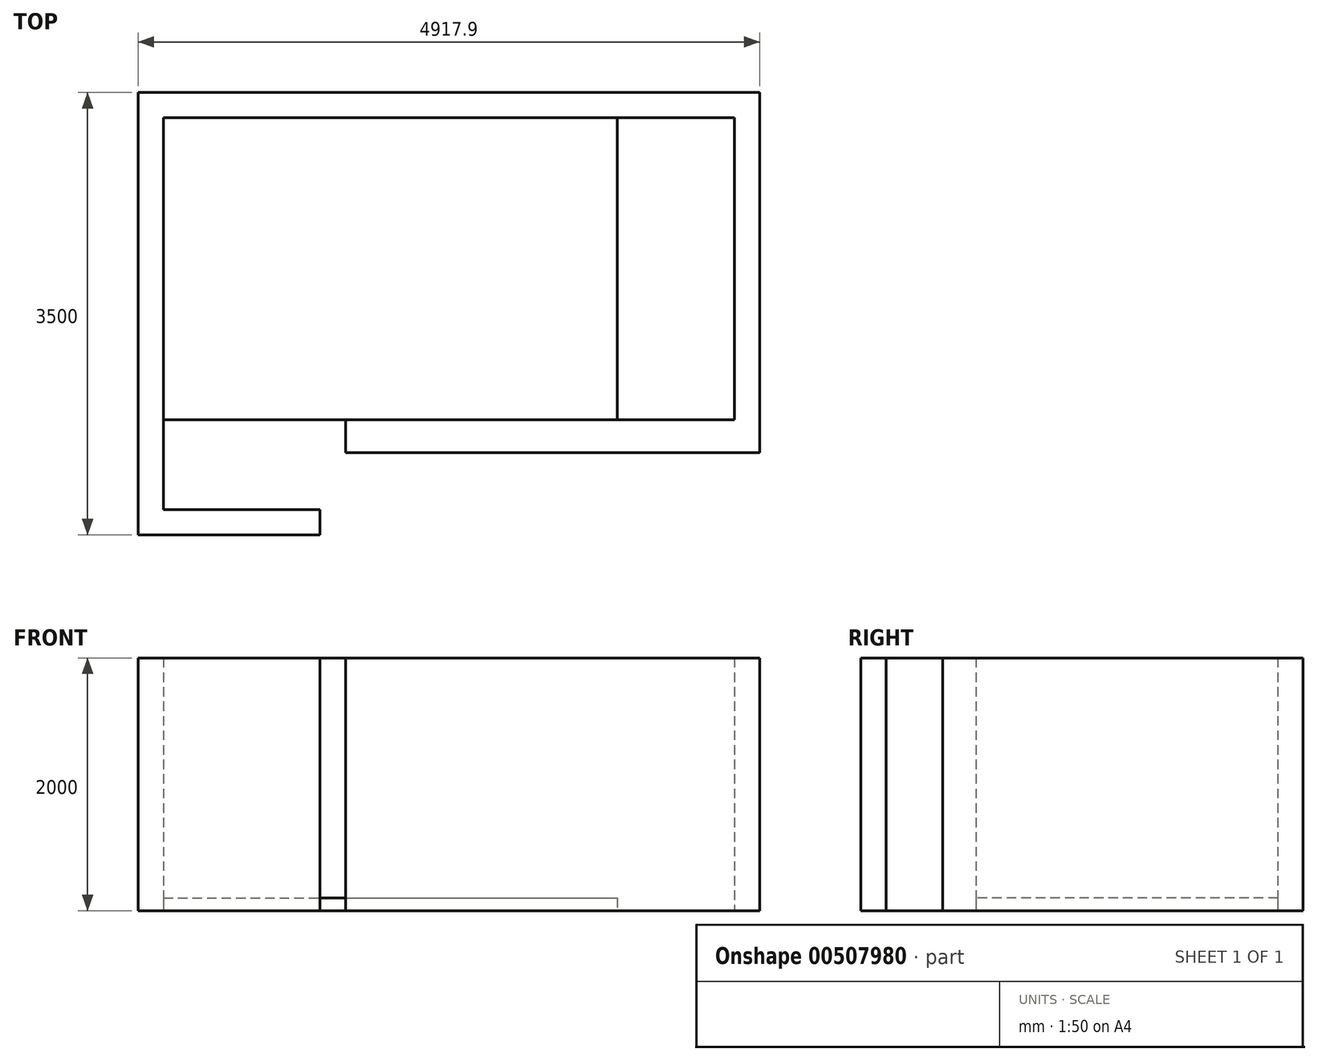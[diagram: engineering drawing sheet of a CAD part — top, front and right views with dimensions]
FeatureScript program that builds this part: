
annotation { "Feature Type Name" : "Feature", "Feature Type Description" : "" }
export const myFeature = defineFeature(function(context is Context, id is Id, definition is map)
    precondition{}
    {
        {
            var Q0;
            Q0=qCreatedBy(makeId("Top.planeOp"),FACE);
            var sketch = newSketch(context, id + "F0", { "sketchPlane" : qUnion([Q0])});
            skLineSegment(sketch, "E0.bottom", {"start": v(-1795, 1195) * mm, "end": v(1795, 1195) * mm});
            skLineSegment(sketch, "E0.top", {"start": v(-1795, -1195) * mm, "end": v(1795, -1195) * mm});
            skLineSegment(sketch, "E0.left", {"start": v(-1795, 1195) * mm, "end": v(-1795, -1195) * mm});
            skLineSegment(sketch, "E0.right", {"start": v(1795, 1195) * mm, "end": v(1795, -1195) * mm});
            skPoint(sketch, "E0.middle", {"position": v(0, 0) * mm});
            skLineSegment(sketch, "E1.bottom", {"start": v(-1795, -1195) * mm, "end": v(-555, -1195) * mm});
            skLineSegment(sketch, "E1.top", {"start": v(-1795, -1905) * mm, "end": v(-555, -1905) * mm});
            skLineSegment(sketch, "E1.left", {"start": v(-1795, -1195) * mm, "end": v(-1795, -1905) * mm});
            skLineSegment(sketch, "E1.right", {"start": v(-555, -1195) * mm, "end": v(-555, -1905) * mm});
            skLineSegment(sketch, "E2.bottom", {"start": v(-1795, 1195) * mm, "end": v(-1995, 1195) * mm});
            skLineSegment(sketch, "E2.top", {"start": v(-1795, -1905) * mm, "end": v(-1995, -1905) * mm});
            skLineSegment(sketch, "E2.left", {"start": v(-1795, 1195) * mm, "end": v(-1795, -1905) * mm});
            skLineSegment(sketch, "E2.right", {"start": v(-1995, 1195) * mm, "end": v(-1995, -1905) * mm});
            skLineSegment(sketch, "E3.bottom", {"start": v(-1995, -1905) * mm, "end": v(-555, -1905) * mm});
            skLineSegment(sketch, "E3.top", {"start": v(-1995, -2105) * mm, "end": v(-555, -2105) * mm});
            skLineSegment(sketch, "E3.left", {"start": v(-1995, -1905) * mm, "end": v(-1995, -2105) * mm});
            skLineSegment(sketch, "E3.right", {"start": v(-555, -1905) * mm, "end": v(-555, -2105) * mm});
            skLineSegment(sketch, "E4.bottom", {"start": v(-555, -1195) * mm, "end": v(-355, -1195) * mm});
            skLineSegment(sketch, "E4.top", {"start": v(-555, -2105) * mm, "end": v(-355, -2105) * mm});
            skLineSegment(sketch, "E4.left", {"start": v(-555, -1195) * mm, "end": v(-555, -2105) * mm});
            skLineSegment(sketch, "E4.right", {"start": v(-355, -1195) * mm, "end": v(-355, -2105) * mm});
            skLineSegment(sketch, "E5.bottom", {"start": v(-355, -1195) * mm, "end": v(2722.9, -1195) * mm});
            skLineSegment(sketch, "E5.top", {"start": v(-355, -1456.6) * mm, "end": v(2722.9, -1456.6) * mm});
            skLineSegment(sketch, "E5.left", {"start": v(-355, -1195) * mm, "end": v(-355, -1456.6) * mm});
            skLineSegment(sketch, "E5.right", {"start": v(2722.9, -1195) * mm, "end": v(2722.9, -1456.6) * mm});
            skLineSegment(sketch, "E6.bottom", {"start": v(2722.9, -1456.6) * mm, "end": v(2922.9, -1456.6) * mm});
            skLineSegment(sketch, "E6.top", {"start": v(2722.9, 1195) * mm, "end": v(2922.9, 1195) * mm});
            skLineSegment(sketch, "E6.left", {"start": v(2722.9, -1456.6) * mm, "end": v(2722.9, 1195) * mm});
            skLineSegment(sketch, "E6.right", {"start": v(2922.9, -1456.6) * mm, "end": v(2922.9, 1195) * mm});
            skLineSegment(sketch, "E7.bottom", {"start": v(-1995, 1195) * mm, "end": v(2922.9, 1195) * mm});
            skLineSegment(sketch, "E7.top", {"start": v(-1995, 1395) * mm, "end": v(2922.9, 1395) * mm});
            skLineSegment(sketch, "E7.left", {"start": v(-1995, 1195) * mm, "end": v(-1995, 1395) * mm});
            skLineSegment(sketch, "E7.right", {"start": v(2922.9, 1195) * mm, "end": v(2922.9, 1395) * mm});
            skSolve(sketch);
        }
        {
            var Q0;
            {var subQ3=sQuery(id+"F0.wireOp",EDGE,"E2.right");Q0=makeQuery(id+"F0.imprint","IMPRINT",FACE,{"disambiguationData":[TD([[makeQuery(id+"F0.imprint","IMPRINT",EDGE,{"derivedFrom":subQ3}),1.0]])]});}
            extrude(context, id + "F1", {"entities" : qUnion([Q0]), "depth" : 2000 * mm});
        }
        {
            var Q0;
            {var subQ1=sQuery(id+"F0.wireOp",EDGE,"E3.top");Q0=makeQuery(id+"F0.imprint","IMPRINT",FACE,{"disambiguationData":[TD([[makeQuery(id+"F0.imprint","IMPRINT",EDGE,{"derivedFrom":subQ1}),1.0]])]});}
            var Q1;
            {var subQ3=sQuery(id+"F0.wireOp",EDGE,"E4.bottom");Q1=makeQuery(id+"F0.imprint","IMPRINT",FACE,{"disambiguationData":[TD([[makeQuery(id+"F0.imprint","IMPRINT",EDGE,{"derivedFrom":subQ3}),-1.0]])]});}
            var Q2;
            {var subQ1=sQuery(id+"F0.wireOp",EDGE,"E5.top");Q2=makeQuery(id+"F0.imprint","IMPRINT",FACE,{"disambiguationData":[TD([[makeQuery(id+"F0.imprint","IMPRINT",EDGE,{"derivedFrom":subQ1}),1.0]])]});}
            var Q3;
            {var subQ5=sQuery(id+"F0.wireOp",EDGE,"E6.bottom");Q3=makeQuery(id+"F0.imprint","IMPRINT",FACE,{"disambiguationData":[TD([[makeQuery(id+"F0.imprint","IMPRINT",EDGE,{"derivedFrom":subQ5}),1.0]])]});}
            var Q4;
            Q4=makeQuery(id+"F0.imprint","IMPRINT",FACE,{"disambiguationData":[TD([[makeQuery(id+"F0.imprint","IMPRINT",EDGE,{"derivedFrom":sQuery(id+"F0.wireOp",EDGE,"E7.top")}),-1.0]])]});
            extrude(context, id + "F2", {"entities" : qUnion([Q0, Q1, Q2, Q3, Q4]), "operationType" : NewBodyOperationType.ADD, "depth" : 2000 * mm});
        }
        {
            var Q0;
            {var subQ0=sQuery(id+"F0.wireOp",EDGE,"E1.bottom");Q0=makeQuery(id+"F0.imprint","IMPRINT",FACE,{"disambiguationData":[TD([[makeQuery(id+"F0.imprint","IMPRINT",EDGE,{"derivedFrom":subQ0}),-1.0]])]});}
            var Q1;
            {var subQ5=sQuery(id+"F0.wireOp",EDGE,"E0.right");Q1=makeQuery(id+"F0.imprint","IMPRINT",FACE,{"disambiguationData":[TD([[makeQuery(id+"F0.imprint","IMPRINT",EDGE,{"derivedFrom":subQ5}),-1.0]])]});}
            extrude(context, id + "F3", {"entities" : qUnion([Q0, Q1]), "operationType" : NewBodyOperationType.ADD, "depth" : 100 * mm});
        }
    });
